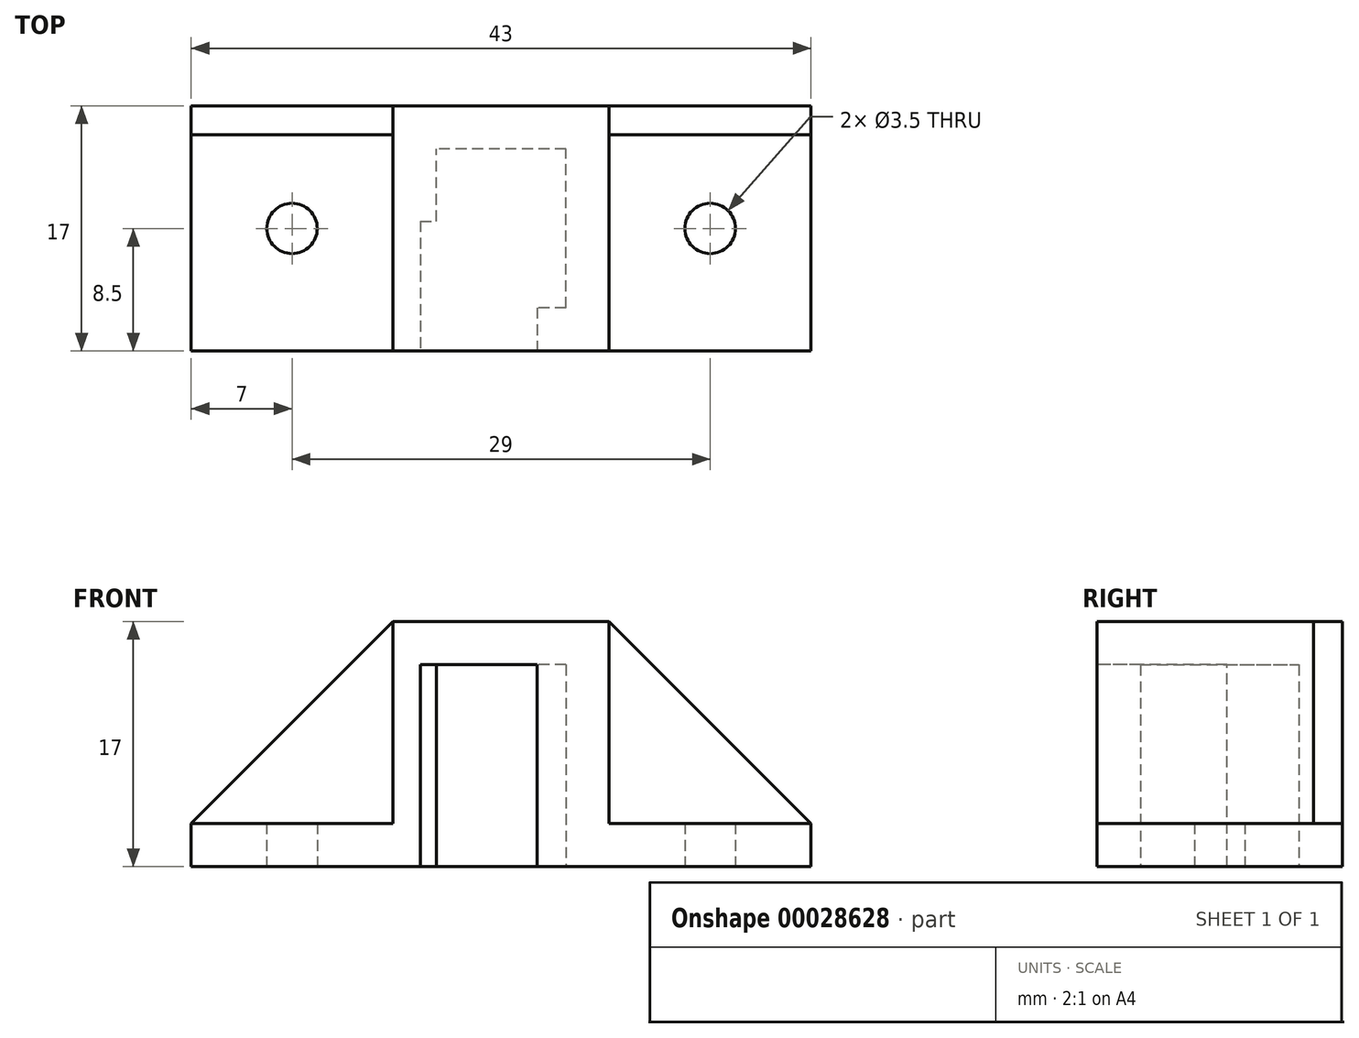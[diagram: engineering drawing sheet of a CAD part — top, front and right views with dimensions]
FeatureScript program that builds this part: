
annotation { "Feature Type Name" : "Feature", "Feature Type Description" : "" }
export const myFeature = defineFeature(function(context is Context, id is Id, definition is map)
    precondition{}
    {
        {
            var Q0;
            Q0=qCreatedBy(makeId("Top.planeOp"),FACE);
            var sketch = newSketch(context, id + "F0", { "sketchPlane" : qUnion([Q0])});
            skLineSegment(sketch, "E0.rect.bottom", {"start": v(4.5, -5.5) * mm, "end": v(-4.5, -5.5) * mm});
            skLineSegment(sketch, "E0.rect.top", {"start": v(4.5, 5.5) * mm, "end": v(-4.5, 5.5) * mm});
            skLineSegment(sketch, "E0.rect.left", {"start": v(4.5, -5.5) * mm, "end": v(4.5, 5.5) * mm});
            skLineSegment(sketch, "E0.rect.right", {"start": v(-4.5, -5.5) * mm, "end": v(-4.5, 5.5) * mm});
            skPoint(sketch, "E0.rect.middle", {"position": v(0, 0) * mm});
            skLineSegment(sketch, "E1.rect.bottom", {"start": v(7.5, -8.5) * mm, "end": v(-7.5, -8.5) * mm});
            skLineSegment(sketch, "E1.rect.top", {"start": v(7.5, 8.5) * mm, "end": v(-7.5, 8.5) * mm});
            skLineSegment(sketch, "E1.rect.left", {"start": v(7.5, -8.5) * mm, "end": v(7.5, 8.5) * mm});
            skLineSegment(sketch, "E1.rect.right", {"start": v(-7.5, -8.5) * mm, "end": v(-7.5, 8.5) * mm});
            skSolve(sketch);
        }
        {
            var Q0;
            Q0=makeQuery(id+"F0.imprint","IMPRINT",FACE,{"disambiguationData":[TD([[makeQuery(id+"F0.imprint","IMPRINT",EDGE,{"derivedFrom":sQuery(id+"F0.wireOp",EDGE,"E0.rect.bottom")}),1.0]])]});
            extrude(context, id + "F1", {"entities" : qUnion([Q0]), "depth" : 17 * mm});
        }
        {
            var Q0;
            Q0=qCreatedBy(makeId("Top.planeOp"),FACE);
            var sketch = newSketch(context, id + "F2", { "sketchPlane" : qUnion([Q0])});
            skLineSegment(sketch, "E2.rect.bottom", {"start": v(21.5, 8.5) * mm, "end": v(-21.5, 8.5) * mm});
            skLineSegment(sketch, "E2.rect.top", {"start": v(21.5, -8.5) * mm, "end": v(-21.5, -8.5) * mm});
            skLineSegment(sketch, "E2.rect.left", {"start": v(21.5, 8.5) * mm, "end": v(21.5, -8.5) * mm});
            skLineSegment(sketch, "E2.rect.right", {"start": v(-21.5, 8.5) * mm, "end": v(-21.5, -8.5) * mm});
            skPoint(sketch, "E2.rect.middle", {"position": v(0, 0) * mm});
            skLineSegment(sketch, "E3.rect.bottom", {"start": v(7.5, 8.5) * mm, "end": v(-7.5, 8.5) * mm});
            skLineSegment(sketch, "E3.rect.top", {"start": v(7.5, -8.5) * mm, "end": v(-7.5, -8.5) * mm});
            skLineSegment(sketch, "E3.rect.left", {"start": v(7.5, 8.5) * mm, "end": v(7.5, -8.5) * mm});
            skLineSegment(sketch, "E3.rect.right", {"start": v(-7.5, 8.5) * mm, "end": v(-7.5, -8.5) * mm});
            skSolve(sketch);
        }
        {
            var Q0;
            {var subQ1=sQuery(id+"F2.wireOp",EDGE,"E2.rect.right");Q0=makeQuery(id+"F2.imprint","IMPRINT",FACE,{"disambiguationData":[TD([[makeQuery(id+"F2.imprint","IMPRINT",EDGE,{"derivedFrom":subQ1}),1.0]])]});}
            var Q1;
            {var subQ1=sQuery(id+"F2.wireOp",EDGE,"E2.rect.left");Q1=makeQuery(id+"F2.imprint","IMPRINT",FACE,{"disambiguationData":[TD([[makeQuery(id+"F2.imprint","IMPRINT",EDGE,{"derivedFrom":subQ1}),-1.0]])]});}
            extrude(context, id + "F3", {"entities" : qUnion([Q0, Q1]), "operationType" : NewBodyOperationType.ADD, "depth" : 3 * mm});
        }
        {
            var Q0;
            {var subQ0=sQuery(id+"F2.wireOp",EDGE,"E2.rect.bottom");Q0=makeQuery(id+"F3.boolean.opBoolean","MERGE",FACE,{"derivedFrom":[makeQuery(id+"F1.opExtrude","SWEPT_FACE",FACE,{"disambiguationData":[OSD([sQuery(id+"F0.wireOp",EDGE,"E1.rect.top")])]}),makeQuery(id+"F3.opExtrude","SWEPT_FACE",FACE,{"disambiguationData":[OSD([subQ0]),TDD([makeQuery(id+"F2.imprint","IMPRINT",EDGE,{"disambiguationData":[TD([[makeQuery(id+"F2.imprint","INTERSECT",VERTEX,{"derivedFrom":[subQ0,sQuery(id+"F2.wireOp",EDGE,"E2.rect.left")]}),-1.0]])],"derivedFrom":subQ0})])]}),makeQuery(id+"F3.opExtrude","SWEPT_FACE",FACE,{"disambiguationData":[OSD([subQ0]),TDD([makeQuery(id+"F2.imprint","IMPRINT",EDGE,{"disambiguationData":[TD([[makeQuery(id+"F2.imprint","INTERSECT",VERTEX,{"derivedFrom":[subQ0,sQuery(id+"F2.wireOp",EDGE,"E2.rect.right")]}),1.0]])],"derivedFrom":subQ0})])]})]});}
            var sketch = newSketch(context, id + "F4", { "sketchPlane" : qUnion([Q0])});
            skLineSegment(sketch, "E4", {"start": v(-21.5, 3) * mm, "end": v(-7.5, 17) * mm});
            skLineSegment(sketch, "E5", {"start": v(-7.5, 17) * mm, "end": v(-7.5, 3) * mm});
            skLineSegment(sketch, "E6", {"start": v(-7.5, 3) * mm, "end": v(-21.5, 3) * mm});
            skLineSegment(sketch, "E7", {"start": v(7.5, 3) * mm, "end": v(7.5, 17) * mm});
            skLineSegment(sketch, "E8", {"start": v(7.5, 17) * mm, "end": v(21.5, 3) * mm});
            skLineSegment(sketch, "E9", {"start": v(21.5, 3) * mm, "end": v(7.5, 3) * mm});
            skSolve(sketch);
        }
        {
            var Q0;
            Q0 = qSketchRegion(id + "F4", true);
            extrude(context, id + "F5", {"entities" : qUnion([Q0]), "operationType" : NewBodyOperationType.ADD, "oppositeDirection" : true, "depth" : 2 * mm});
        }
        {
            var Q0;
            Q0=makeQuery(id+"F1.opExtrude","SWEPT_FACE",FACE,{"disambiguationData":[OSD([sQuery(id+"F0.wireOp",EDGE,"E0.rect.bottom")])]});
            var sketch = newSketch(context, id + "F6", { "sketchPlane" : qUnion([Q0])});
            skLineSegment(sketch, "E10.bottom", {"start": v(4.5, 17) * mm, "end": v(-2.5, 17) * mm});
            skLineSegment(sketch, "E10.top", {"start": v(4.5, 0) * mm, "end": v(-2.5, 0) * mm});
            skLineSegment(sketch, "E10.left", {"start": v(4.5, 17) * mm, "end": v(4.5, 0) * mm});
            skLineSegment(sketch, "E10.right", {"start": v(-2.5, 17) * mm, "end": v(-2.5, 0) * mm});
            skSolve(sketch);
        }
        {
            var Q0;
            Q0 = qSketchRegion(id + "F6", true);
            extrude(context, id + "F7", {"entities" : qUnion([Q0]), "operationType" : NewBodyOperationType.REMOVE, "oppositeDirection" : true, "depth" : 25 * mm});
        }
        {
            var Q0;
            Q0=makeQuery(id+"F1.opExtrude","CAP_FACE",FACE,{"disambiguationData":[OSD([sQuery(id+"F0.wireOp",EDGE,"E0.rect.bottom"),sQuery(id+"F0.wireOp",EDGE,"E0.rect.top"),sQuery(id+"F0.wireOp",EDGE,"E0.rect.left"),sQuery(id+"F0.wireOp",EDGE,"E0.rect.right"),sQuery(id+"F0.wireOp",EDGE,"E1.rect.bottom"),sQuery(id+"F0.wireOp",EDGE,"E1.rect.top"),sQuery(id+"F0.wireOp",EDGE,"E1.rect.left"),sQuery(id+"F0.wireOp",EDGE,"E1.rect.right")])],"isStart":false});
            var sketch = newSketch(context, id + "F8", { "sketchPlane" : qUnion([Q0])});
            skLineSegment(sketch, "E11.bottom", {"start": v(-4.5, -8.5) * mm, "end": v(-5.6, -8.5) * mm});
            skLineSegment(sketch, "E11.top", {"start": v(-4.5, 0.5) * mm, "end": v(-5.6, 0.5) * mm});
            skLineSegment(sketch, "E11.left", {"start": v(-4.5, -8.5) * mm, "end": v(-4.5, 0.5) * mm});
            skLineSegment(sketch, "E11.right", {"start": v(-5.6, -8.5) * mm, "end": v(-5.6, 0.5) * mm});
            skSolve(sketch);
        }
        {
            var Q0;
            Q0 = qSketchRegion(id + "F8", true);
            extrude(context, id + "F9", {"entities" : qUnion([Q0]), "operationType" : NewBodyOperationType.REMOVE, "oppositeDirection" : true, "depth" : 25 * mm});
        }
        {
            var Q0;
            Q0=makeQuery(id+"F1.opExtrude","CAP_FACE",FACE,{"disambiguationData":[OSD([sQuery(id+"F0.wireOp",EDGE,"E0.rect.bottom"),sQuery(id+"F0.wireOp",EDGE,"E0.rect.top"),sQuery(id+"F0.wireOp",EDGE,"E0.rect.left"),sQuery(id+"F0.wireOp",EDGE,"E0.rect.right"),sQuery(id+"F0.wireOp",EDGE,"E1.rect.bottom"),sQuery(id+"F0.wireOp",EDGE,"E1.rect.top"),sQuery(id+"F0.wireOp",EDGE,"E1.rect.left"),sQuery(id+"F0.wireOp",EDGE,"E1.rect.right")])],"isStart":false});
            var sketch = newSketch(context, id + "F10", { "sketchPlane" : qUnion([Q0])});
            skLineSegment(sketch, "E12.bottom", {"start": v(-7.5, 8.5) * mm, "end": v(7.5, 8.5) * mm});
            skLineSegment(sketch, "E12.top", {"start": v(-7.5, -8.5) * mm, "end": v(7.5, -8.5) * mm});
            skLineSegment(sketch, "E12.left", {"start": v(-7.5, 8.5) * mm, "end": v(-7.5, -8.5) * mm});
            skLineSegment(sketch, "E12.right", {"start": v(7.5, 8.5) * mm, "end": v(7.5, -8.5) * mm});
            skSolve(sketch);
        }
        {
            var Q0;
            Q0 = qSketchRegion(id + "F10", true);
            extrude(context, id + "F11", {"entities" : qUnion([Q0]), "operationType" : NewBodyOperationType.ADD, "oppositeDirection" : true, "depth" : 3 * mm});
        }
        {
            var Q0;
            {var subQ0=sQuery(id+"F2.wireOp",EDGE,"E2.rect.bottom");var subQ1=sQuery(id+"F2.wireOp",EDGE,"E2.rect.top");Q0=makeQuery(id+"F3.boolean.opBoolean","MERGE",FACE,{"derivedFrom":[makeQuery(id+"F1.opExtrude","CAP_FACE",FACE,{"disambiguationData":[OSD([sQuery(id+"F0.wireOp",EDGE,"E0.rect.bottom"),sQuery(id+"F0.wireOp",EDGE,"E0.rect.top"),sQuery(id+"F0.wireOp",EDGE,"E0.rect.left"),sQuery(id+"F0.wireOp",EDGE,"E0.rect.right"),sQuery(id+"F0.wireOp",EDGE,"E1.rect.bottom"),sQuery(id+"F0.wireOp",EDGE,"E1.rect.top"),sQuery(id+"F0.wireOp",EDGE,"E1.rect.left"),sQuery(id+"F0.wireOp",EDGE,"E1.rect.right")])],"isStart":true}),makeQuery(id+"F3.opExtrude","CAP_FACE",FACE,{"disambiguationData":[OSD([subQ0,subQ1,sQuery(id+"F2.wireOp",EDGE,"E2.rect.left"),sQuery(id+"F2.wireOp",EDGE,"E3.rect.left")])],"isStart":true}),makeQuery(id+"F3.opExtrude","CAP_FACE",FACE,{"disambiguationData":[OSD([subQ0,subQ1,sQuery(id+"F2.wireOp",EDGE,"E2.rect.right"),sQuery(id+"F2.wireOp",EDGE,"E3.rect.right")])],"isStart":true})]});}
            var sketch = newSketch(context, id + "F12", { "sketchPlane" : qUnion([Q0])});
            skLineSegment(sketch, "E13", {"start": v(-21.5, 0) * mm, "end": v(-7.5, 0) * mm, "construction": true});
            skLineSegment(sketch, "E14", {"start": v(7.5, 0) * mm, "end": v(21.5, 0) * mm, "construction": true});
            skCircle(sketch, "E15", {"center": v(-14.5, 0) * mm, "radius": 1.75 * mm});
            skCircle(sketch, "E16", {"center": v(14.5, 0) * mm, "radius": 1.75 * mm});
            skSolve(sketch);
        }
        {
            var Q0;
            Q0 = qSketchRegion(id + "F12", true);
            extrude(context, id + "F13", {"entities" : qUnion([Q0]), "operationType" : NewBodyOperationType.REMOVE, "oppositeDirection" : true, "depth" : 25 * mm});
        }
    });
